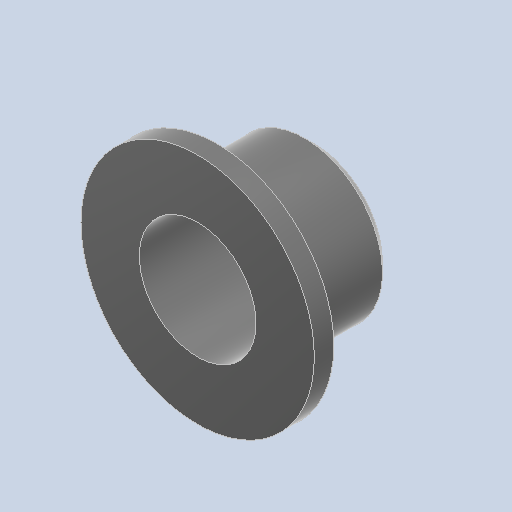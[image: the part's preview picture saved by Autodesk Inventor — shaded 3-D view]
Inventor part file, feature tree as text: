
AUTODESK INVENTOR PART (.ipt)
format: ipt  version: 2023 (Build 270158030, 158C)  size: 119,808 bytes
history: native  units: mm
features: extrude x2, sketch x2, chamfer x1
ambient origin geometry x8: Origin, YZ Plane, XZ Plane, XY Plane, X Axis, Y Axis, Z Axis, Center Point
bodies: Solid1 (feature_tree)
feature tree (5):
  extrude  "Extrusion1"  Depth=6.0mm
  extrude  "Extrusion2"  Depth=5.0mm
  chamfer  "Chamfer1"  Distance=5.0mm
  sketch  "Sketch1"  dims[d0=6.0mm d1=12.0mm]
  sketch  "Sketch2"  dims[d2=1.0mm d3=0.0mm d4=8.0mm d5=5.0mm d6=0.0mm d7=0.5mm d8=2.0mm d9=45.0deg]
